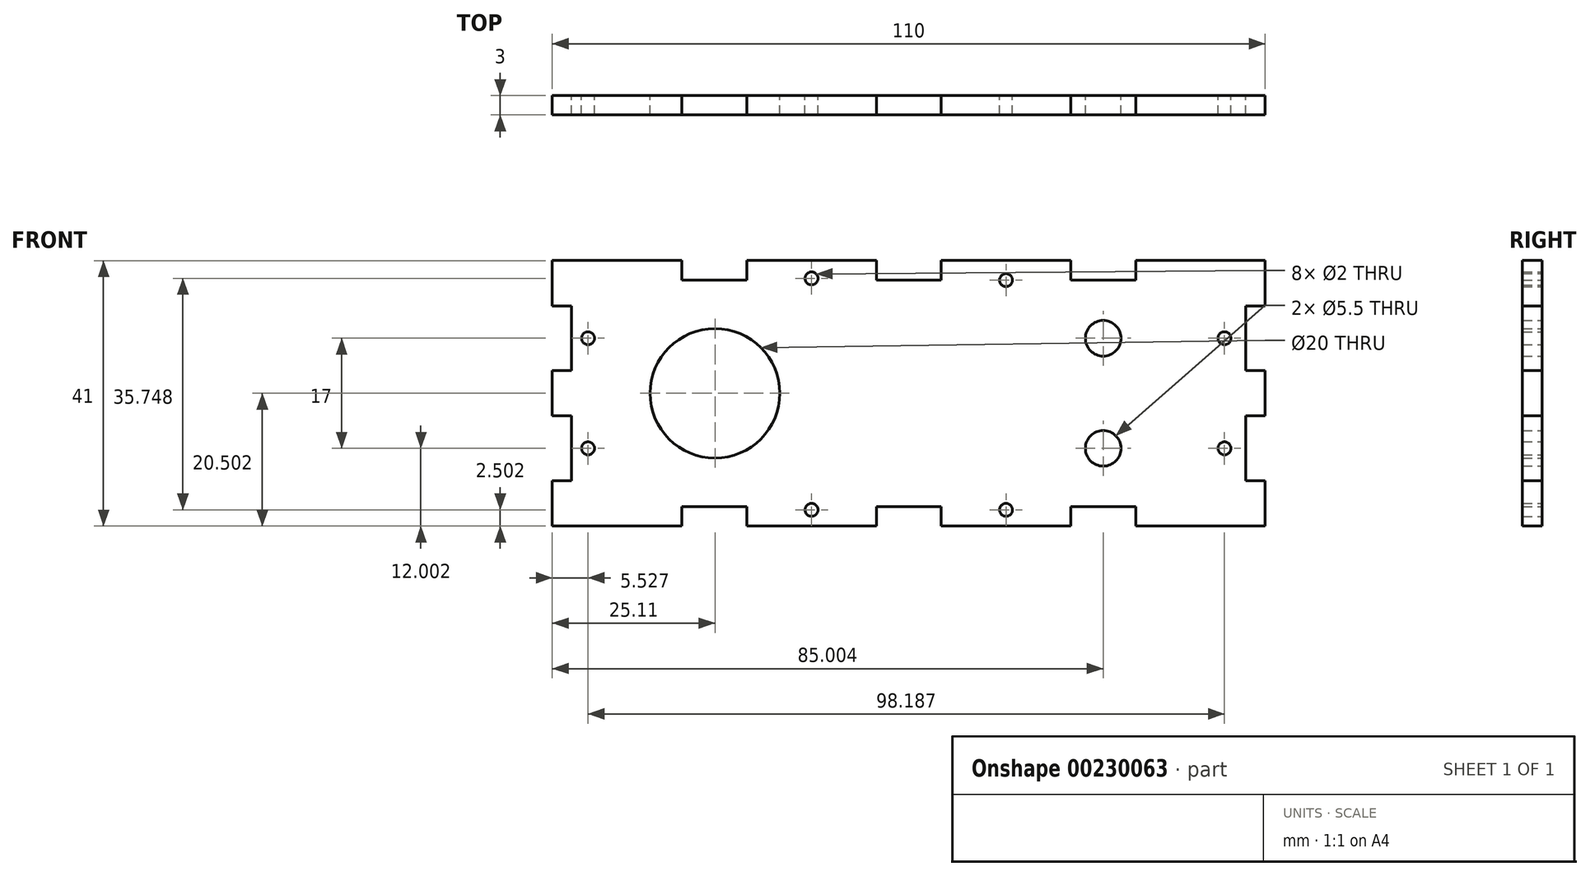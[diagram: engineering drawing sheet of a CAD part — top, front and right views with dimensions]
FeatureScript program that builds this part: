
annotation { "Feature Type Name" : "Feature", "Feature Type Description" : "" }
export const myFeature = defineFeature(function(context is Context, id is Id, definition is map)
    precondition{}
    {
        {
            var Q0;
            Q0=qCreatedBy(makeId("Front.planeOp"),FACE);
            var sketch = newSketch(context, id + "F0", { "sketchPlane" : qUnion([Q0])});
            skLineSegment(sketch, "E0", {"start": v(-54.98, 2.6) * mm, "end": v(-51.98, 2.6) * mm});
            skLineSegment(sketch, "E1", {"start": v(-51.98, 2.6) * mm, "end": v(-51.98, 12.6) * mm});
            skLineSegment(sketch, "E2", {"start": v(-51.98, 12.6) * mm, "end": v(-54.98, 12.6) * mm});
            skLineSegment(sketch, "E3", {"start": v(-54.98, 12.6) * mm, "end": v(-54.98, 19.6) * mm});
            skLineSegment(sketch, "E4", {"start": v(-54.98, 19.6) * mm, "end": v(-34.98, 19.6) * mm});
            skLineSegment(sketch, "E5", {"start": v(-34.98, 19.6) * mm, "end": v(-34.98, 16.6) * mm});
            skLineSegment(sketch, "E6", {"start": v(-34.98, 16.6) * mm, "end": v(-24.98, 16.6) * mm});
            skLineSegment(sketch, "E7", {"start": v(-24.98, 16.6) * mm, "end": v(-24.98, 19.6) * mm});
            skLineSegment(sketch, "E8", {"start": v(-4.98, 19.6) * mm, "end": v(-24.98, 19.6) * mm});
            skLineSegment(sketch, "E9", {"start": v(-4.98, 19.6) * mm, "end": v(-4.98, 16.6) * mm});
            skLineSegment(sketch, "E10", {"start": v(0.02, 16.6) * mm, "end": v(-4.98, 16.6) * mm});
            skCircle(sketch, "E11", {"center": v(-14.98, 16.84) * mm, "radius": 1 * mm});
            skCircle(sketch, "E12", {"center": v(-49.45, 7.6) * mm, "radius": 1 * mm});
            skCircle(sketch, "E13.MirrorC", {"center": v(15.02, 16.57) * mm, "radius": 1 * mm});
            skLineSegment(sketch, "E14", {"start": v(-54.98, 2.6) * mm, "end": v(-54.98, -0.9) * mm});
            skLineSegment(sketch, "E15.MirrorCS", {"start": v(52.02, 12.6) * mm, "end": v(55.02, 12.6) * mm});
            skLineSegment(sketch, "E16.MirrorCS", {"start": v(5.02, 19.6) * mm, "end": v(5.02, 16.6) * mm});
            skLineSegment(sketch, "E17.MirrorCS", {"start": v(35.02, 19.6) * mm, "end": v(35.02, 16.6) * mm});
            skLineSegment(sketch, "E18.MirrorCS", {"start": v(55.02, 2.6) * mm, "end": v(52.02, 2.6) * mm});
            skLineSegment(sketch, "E19.MirrorCS", {"start": v(25.02, 16.6) * mm, "end": v(25.02, 19.6) * mm});
            skCircle(sketch, "E20.MirrorC", {"center": v(48.73, 7.6) * mm, "radius": 1 * mm});
            skLineSegment(sketch, "E21.MirrorCS", {"start": v(55.02, 2.6) * mm, "end": v(55.02, -0.9) * mm});
            skLineSegment(sketch, "E22.MirrorCS", {"start": v(55.02, 12.6) * mm, "end": v(55.02, 19.6) * mm});
            skLineSegment(sketch, "E23.MirrorCS", {"start": v(5.02, 19.6) * mm, "end": v(25.02, 19.6) * mm});
            skLineSegment(sketch, "E24.MirrorCS", {"start": v(35.02, 16.6) * mm, "end": v(25.02, 16.6) * mm});
            skLineSegment(sketch, "E25.MirrorCS", {"start": v(52.02, 2.6) * mm, "end": v(52.02, 12.6) * mm});
            skLineSegment(sketch, "E26.MirrorCS", {"start": v(55.02, 19.6) * mm, "end": v(35.02, 19.6) * mm});
            skLineSegment(sketch, "E27", {"start": v(5.02, 16.6) * mm, "end": v(0.02, 16.6) * mm});
            skLineSegment(sketch, "E28.MirrorCS", {"start": v(25.02, -18.4) * mm, "end": v(25.02, -21.4) * mm});
            skLineSegment(sketch, "E29.MirrorCS", {"start": v(-4.98, -21.4) * mm, "end": v(-4.98, -18.4) * mm});
            skLineSegment(sketch, "E30.MirrorCS", {"start": v(-54.98, -4.4) * mm, "end": v(-51.98, -4.4) * mm});
            skLineSegment(sketch, "E31.MirrorCS", {"start": v(-34.98, -21.4) * mm, "end": v(-34.98, -18.4) * mm});
            skLineSegment(sketch, "E32.MirrorCS", {"start": v(35.02, -21.4) * mm, "end": v(35.02, -18.4) * mm});
            skLineSegment(sketch, "E33.MirrorCS", {"start": v(-51.98, -14.4) * mm, "end": v(-54.98, -14.4) * mm});
            skLineSegment(sketch, "E34.MirrorCS", {"start": v(5.02, -21.4) * mm, "end": v(5.02, -18.4) * mm});
            skLineSegment(sketch, "E35.MirrorCS", {"start": v(55.02, -4.4) * mm, "end": v(52.02, -4.4) * mm});
            skLineSegment(sketch, "E36.MirrorCS", {"start": v(-24.98, -18.4) * mm, "end": v(-24.98, -21.4) * mm});
            skLineSegment(sketch, "E37.MirrorCS", {"start": v(52.02, -14.4) * mm, "end": v(55.02, -14.4) * mm});
            skCircle(sketch, "E38.MirrorC", {"center": v(-49.45, -9.4) * mm, "radius": 1 * mm});
            skCircle(sketch, "E39.MirrorC", {"center": v(48.73, -9.4) * mm, "radius": 1 * mm});
            skLineSegment(sketch, "E40.MirrorCS", {"start": v(-51.98, -4.4) * mm, "end": v(-51.98, -14.4) * mm});
            skLineSegment(sketch, "E41.MirrorCS", {"start": v(5.02, -18.4) * mm, "end": v(0.02, -18.4) * mm});
            skLineSegment(sketch, "E42.MirrorCS", {"start": v(35.02, -18.4) * mm, "end": v(25.02, -18.4) * mm});
            skLineSegment(sketch, "E43.MirrorCS", {"start": v(55.02, -21.4) * mm, "end": v(35.02, -21.4) * mm});
            skLineSegment(sketch, "E44.MirrorCS", {"start": v(0.02, -18.4) * mm, "end": v(-4.98, -18.4) * mm});
            skLineSegment(sketch, "E45.MirrorCS", {"start": v(-54.98, -14.4) * mm, "end": v(-54.98, -21.4) * mm});
            skLineSegment(sketch, "E46.MirrorCS", {"start": v(-34.98, -18.4) * mm, "end": v(-24.98, -18.4) * mm});
            skLineSegment(sketch, "E47.MirrorCS", {"start": v(55.02, -14.4) * mm, "end": v(55.02, -21.4) * mm});
            skLineSegment(sketch, "E48.MirrorCS", {"start": v(5.02, -21.4) * mm, "end": v(25.02, -21.4) * mm});
            skLineSegment(sketch, "E49.MirrorCS", {"start": v(52.02, -4.4) * mm, "end": v(52.02, -14.4) * mm});
            skLineSegment(sketch, "E50.MirrorCS", {"start": v(-54.98, -21.4) * mm, "end": v(-34.98, -21.4) * mm});
            skLineSegment(sketch, "E51.MirrorCS", {"start": v(-4.98, -21.4) * mm, "end": v(-24.98, -21.4) * mm});
            skLineSegment(sketch, "E52", {"start": v(-54.98, -0.9) * mm, "end": v(-54.98, -4.4) * mm});
            skLineSegment(sketch, "E53", {"start": v(55.02, -0.9) * mm, "end": v(55.02, -4.4) * mm});
            skPoint(sketch, "E54", {"position": v(52.02, 7.6) * mm});
            skPoint(sketch, "E55", {"position": v(15.02, 19.6) * mm});
            skPoint(sketch, "E56", {"position": v(-14.98, 19.6) * mm});
            skPoint(sketch, "E57", {"position": v(-51.98, 7.6) * mm});
            skCircle(sketch, "E58", {"center": v(-14.98, -18.9) * mm, "radius": 1 * mm});
            skCircle(sketch, "E59", {"center": v(15.02, -18.9) * mm, "radius": 1 * mm});
            skCircle(sketch, "E60", {"center": v(-29.87, -0.9) * mm, "radius": 10 * mm});
            skLineSegment(sketch, "E61", {"start": v(30.02, 16.6) * mm, "end": v(30.02, -18.4) * mm, "construction": true});
            skCircle(sketch, "E62", {"center": v(30.02, 7.6) * mm, "radius": 2.75 * mm});
            skCircle(sketch, "E63", {"center": v(30.02, -9.4) * mm, "radius": 2.75 * mm});
            skSolve(sketch);
        }
        {
            var Q0;
            Q0 = qSketchRegion(id + "F0", true);
            extrude(context, id + "F1", {"entities" : qUnion([Q0]), "depth" : 3 * mm});
        }
    });
